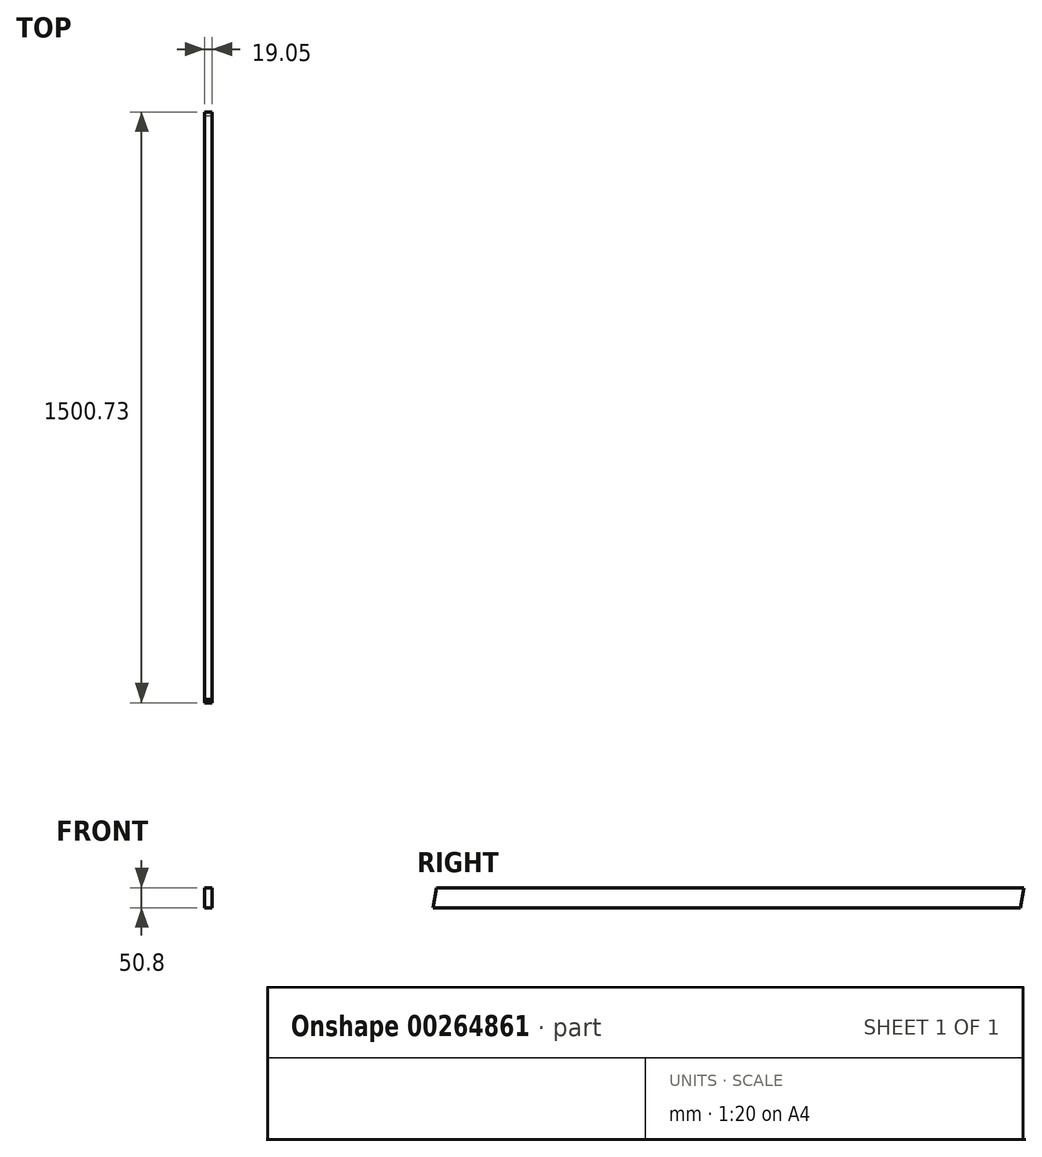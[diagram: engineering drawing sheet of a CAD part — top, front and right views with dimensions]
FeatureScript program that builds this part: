
annotation { "Feature Type Name" : "Feature", "Feature Type Description" : "" }
export const myFeature = defineFeature(function(context is Context, id is Id, definition is map)
    precondition{}
    {
        {
            var Q0;
            Q0=qCreatedBy(makeId("Top.planeOp"),FACE);
            var sketch = newSketch(context, id + "F0", { "sketchPlane" : qUnion([Q0])});
            skLineSegment(sketch, "E0.bottom", {"start": v(0, 0) * mm, "end": v(19.05, 0) * mm});
            skLineSegment(sketch, "E0.top", {"start": v(0, 1500.73) * mm, "end": v(19.05, 1500.73) * mm});
            skLineSegment(sketch, "E0.left", {"start": v(0, 0) * mm, "end": v(0, 1500.73) * mm});
            skLineSegment(sketch, "E0.right", {"start": v(19.05, 0) * mm, "end": v(19.05, 1500.73) * mm});
            skSolve(sketch);
        }
        {
            var Q0;
            Q0=makeQuery(id+"F0.imprint","IMPRINT",FACE,{"disambiguationData":[TD([[makeQuery(id+"F0.imprint","IMPRINT",EDGE,{"derivedFrom":sQuery(id+"F0.wireOp",EDGE,"E0.bottom")}),1.0]])]});
            extrude(context, id + "F1", {"entities" : qUnion([Q0]), "depth" : 50.8 * mm, "offsetDistance" : 25.4 * mm});
        }
        {
            var Q0;
            Q0=makeQuery(id+"F1.opExtrude","SWEPT_FACE",FACE,{"disambiguationData":[OSD([sQuery(id+"F0.wireOp",EDGE,"E0.right")])]});
            var sketch = newSketch(context, id + "F2", { "sketchPlane" : qUnion([Q0])});
            skLineSegment(sketch, "E1", {"start": v(0, 125.8) * mm, "end": v(0, 0) * mm});
            skLineSegment(sketch, "E2", {"start": v(0, 0) * mm, "end": v(22.18, 125.8) * mm});
            skLineSegment(sketch, "E3", {"start": v(22.18, 125.8) * mm, "end": v(0, 125.8) * mm});
            skLineSegment(sketch, "E4", {"start": v(1500.73, 50.8) * mm, "end": v(1500.73, 50.8) * mm});
            skLineSegment(sketch, "E5", {"start": v(1500.73, 50.8) * mm, "end": v(1500.73, -61.64) * mm});
            skLineSegment(sketch, "E6", {"start": v(1500.73, -61.64) * mm, "end": v(1480.9, -61.64) * mm});
            skLineSegment(sketch, "E7", {"start": v(1480.9, -61.64) * mm, "end": v(1500.73, 50.8) * mm});
            skSolve(sketch);
        }
        {
            var Q0;
            {var subQ1=sQuery(id+"F2.wireOp",EDGE,"E1");var subQ2=sQuery(id+"F0.wireOp",EDGE,"E0.right");var subQ4=makeQuery(id+"F1.opExtrude","CAP_EDGE",EDGE,{"disambiguationData":[OSD([subQ2])],"isStart":false});var subQ5=makeQuery(id+"F2.imprint","INTERSECT",VERTEX,{"derivedFrom":[subQ4,subQ1]});Q0=makeQuery(id+"F2.imprint","IMPRINT",FACE,{"disambiguationData":[TD([[makeQuery(id+"F2.imprint","IMPRINT",EDGE,{"disambiguationData":[TD([[subQ5,-1.0]])],"derivedFrom":subQ4}),-1.0]])]});}
            var Q1;
            {var subQ0=sQuery(id+"F2.wireOp",EDGE,"E4");var subQ1=sQuery(id+"F0.wireOp",EDGE,"E0.right");var subQ2=makeQuery(id+"F1.opExtrude","CAP_EDGE",EDGE,{"disambiguationData":[OSD([subQ1])],"isStart":true});var subQ3=makeQuery(id+"F2.imprint","INTERSECT",VERTEX,{"derivedFrom":[subQ2,subQ0]});Q1=makeQuery(id+"F2.imprint","IMPRINT",FACE,{"disambiguationData":[TD([[makeQuery(id+"F2.imprint","IMPRINT",EDGE,{"disambiguationData":[TD([[subQ3,1.0]])],"derivedFrom":subQ2}),1.0]])]});}
            extrude(context, id + "F3", {"entities" : qUnion([Q0, Q1]), "operationType" : NewBodyOperationType.REMOVE, "endBound" : BoundingType.THROUGH_ALL, "oppositeDirection" : true, "depth" : 25.4 * mm, "offsetDistance" : 25.4 * mm});
        }
    });
